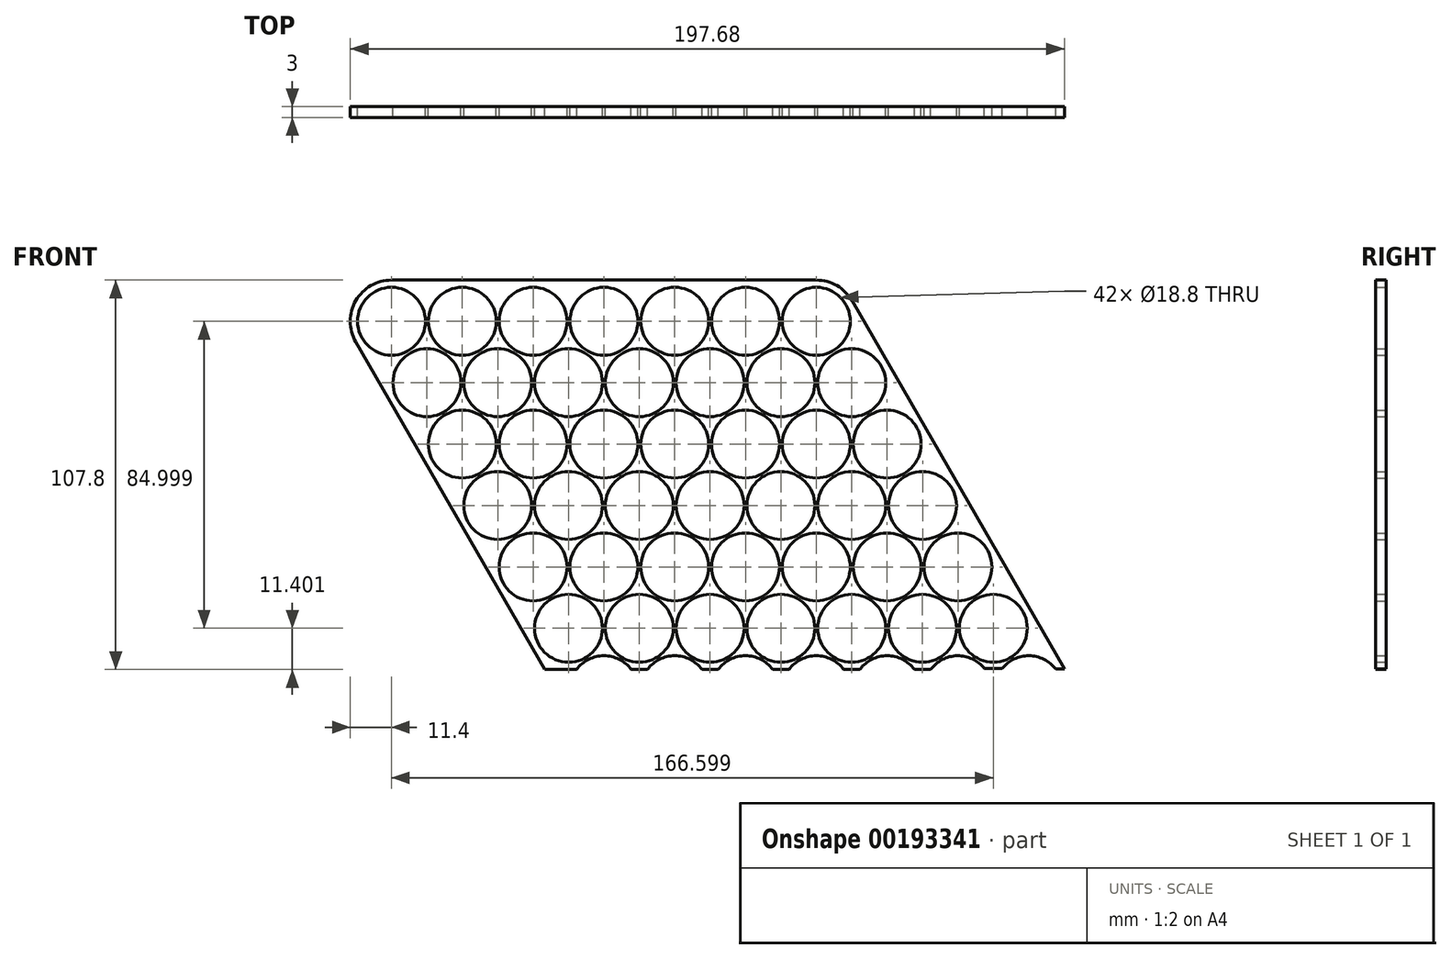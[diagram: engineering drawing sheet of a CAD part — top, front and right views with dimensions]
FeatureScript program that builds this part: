
annotation { "Feature Type Name" : "Feature", "Feature Type Description" : "" }
export const myFeature = defineFeature(function(context is Context, id is Id, definition is map)
    precondition{}
    {
        {
            var Q0;
            Q0=qCreatedBy(makeId("Front.planeOp"),FACE);
            var sketch = newSketch(context, id + "F0", { "sketchPlane" : qUnion([Q0])});
            skCircle(sketch, "E0", {"center": v(0, 0) * mm, "radius": 9.4 * mm});
            skCircle(sketch, "E1.1.0.0", {"center": v(19.6, 0) * mm, "radius": 9.4 * mm});
            skCircle(sketch, "E1.2.0.0", {"center": v(39.2, 0) * mm, "radius": 9.4 * mm});
            skCircle(sketch, "E1.3.0.0", {"center": v(58.8, 0) * mm, "radius": 9.4 * mm});
            skLineSegment(sketch, "E1.direction1", {"start": v(0, 0) * mm, "end": v(19.6, 0) * mm, "construction": true});
            skLineSegment(sketch, "E2", {"start": v(0, -17) * mm, "end": v(73.2, -17) * mm, "construction": true});
            skLineSegment(sketch, "E3", {"start": v(9.8, 0) * mm, "end": v(9.8, -17) * mm, "construction": true});
            skCircle(sketch, "E4", {"center": v(9.8, -17) * mm, "radius": 9.4 * mm});
            skCircle(sketch, "E5.1.0.0", {"center": v(29.4, -17) * mm, "radius": 9.4 * mm});
            skCircle(sketch, "E5.2.0.0", {"center": v(49, -17) * mm, "radius": 9.4 * mm});
            skCircle(sketch, "E5.3.0.0", {"center": v(68.6, -17) * mm, "radius": 9.4 * mm});
            skLineSegment(sketch, "E5.direction1", {"start": v(9.8, -17) * mm, "end": v(29.4, -17) * mm, "construction": true});
            skLineSegment(sketch, "E6", {"start": v(9.8, -17) * mm, "end": v(9.8, -26.4) * mm, "construction": true});
            skLineSegment(sketch, "E7", {"start": v(68.6, -17) * mm, "end": v(68.6, -26.4) * mm, "construction": true});
            skArc(sketch, "E8", {"start": v(58.8, 9.4) * mm, "mid": v(63.5, 8.14) * mm, "end": v(66.94, 4.7) * mm});
            skArc(sketch, "E9", {"start": v(76.74, -12.3) * mm, "mid": v(76.74, -21.7) * mm, "end": v(68.6, -26.4) * mm});
            skArc(sketch, "E10", {"start": v(9.8, -26.4) * mm, "mid": v(5.1, -25.14) * mm, "end": v(1.66, -21.7) * mm});
            skArc(sketch, "E11", {"start": v(-8.14, -4.7) * mm, "mid": v(-8.14, 4.7) * mm, "end": v(0, 9.4) * mm});
            skArc(sketch, "E12.0", {"start": v(0, 11.4) * mm, "mid": v(-9.87, 5.7) * mm, "end": v(-9.88, -5.7) * mm});
            skLineSegment(sketch, "E13.0", {"start": v(0, 11.4) * mm, "end": v(58.8, 11.4) * mm});
            skLineSegment(sketch, "E14.0", {"start": v(-9.88, -5.7) * mm, "end": v(-0.08, -22.7) * mm});
            skArc(sketch, "E15.trimOffspring", {"start": v(9.8, -5.82) * mm, "mid": v(9.87, -5.71) * mm, "end": v(9.93, -5.6) * mm});
            skArc(sketch, "E16.trimOffspring", {"start": v(9.93, -5.6) * mm, "mid": v(9.86, -5.6) * mm, "end": v(9.8, -5.6) * mm});
            skCircle(sketch, "E17.0.4.0", {"center": v(78.4, 0) * mm, "radius": 9.4 * mm});
            skCircle(sketch, "E17.0.5.0", {"center": v(98, 0) * mm, "radius": 9.4 * mm});
            skCircle(sketch, "E18.0.4.0", {"center": v(88.2, -17) * mm, "radius": 9.4 * mm});
            skCircle(sketch, "E18.0.5.0", {"center": v(107.8, -17) * mm, "radius": 9.4 * mm});
            skLineSegment(sketch, "E19", {"start": v(58.8, 11.4) * mm, "end": v(98, 11.4) * mm});
            skLineSegment(sketch, "E20", {"start": v(0, 0) * mm, "end": v(9.8, -17) * mm, "construction": true});
            skCircle(sketch, "E21.1.0.0", {"center": v(19.6, -34) * mm, "radius": 9.4 * mm});
            skCircle(sketch, "E21.2.0.0", {"center": v(29.4, -51) * mm, "radius": 9.4 * mm});
            skLineSegment(sketch, "E21.direction1", {"start": v(9.8, -17) * mm, "end": v(19.6, -34) * mm, "construction": true});
            skCircle(sketch, "E22.1.0.0", {"center": v(39.2, -34) * mm, "radius": 9.4 * mm});
            skCircle(sketch, "E22.1.0.1", {"center": v(49, -51) * mm, "radius": 9.4 * mm});
            skCircle(sketch, "E22.2.0.0", {"center": v(58.8, -34) * mm, "radius": 9.4 * mm});
            skCircle(sketch, "E22.2.0.1", {"center": v(68.6, -51) * mm, "radius": 9.4 * mm});
            skCircle(sketch, "E22.3.0.0", {"center": v(78.4, -34) * mm, "radius": 9.4 * mm});
            skCircle(sketch, "E22.3.0.1", {"center": v(88.2, -51) * mm, "radius": 9.4 * mm});
            skCircle(sketch, "E22.4.0.0", {"center": v(98, -34) * mm, "radius": 9.4 * mm});
            skCircle(sketch, "E22.4.0.1", {"center": v(107.8, -51) * mm, "radius": 9.4 * mm});
            skCircle(sketch, "E22.5.0.0", {"center": v(117.6, -34) * mm, "radius": 9.4 * mm});
            skCircle(sketch, "E22.5.0.1", {"center": v(127.4, -51) * mm, "radius": 9.4 * mm});
            skLineSegment(sketch, "E22.direction1", {"start": v(19.6, -34) * mm, "end": v(39.2, -34) * mm, "construction": true});
            skLineSegment(sketch, "E23", {"start": v(-0.08, -22.7) * mm, "end": v(19.52, -56.7) * mm});
            skArc(sketch, "E24.0", {"start": v(29.27, -62.4) * mm, "mid": v(29.33, -62.4) * mm, "end": v(29.4, -62.4) * mm});
            skCircle(sketch, "E25.0.6.0", {"center": v(117.6, 0) * mm, "radius": 9.4 * mm});
            skCircle(sketch, "E26.0.6.0", {"center": v(127.4, -17) * mm, "radius": 9.4 * mm});
            skCircle(sketch, "E27.0.6.0", {"center": v(137.2, -34) * mm, "radius": 9.4 * mm});
            skCircle(sketch, "E27.2.6.0", {"center": v(147, -51) * mm, "radius": 9.4 * mm});
            skLineSegment(sketch, "E28", {"start": v(98, 11.4) * mm, "end": v(117.6, 11.4) * mm});
            skCircle(sketch, "E29.0.3.0", {"center": v(39.2, -68) * mm, "radius": 9.4 * mm});
            skCircle(sketch, "E30.1.0.0", {"center": v(58.8, -68) * mm, "radius": 9.4 * mm});
            skCircle(sketch, "E30.2.0.0", {"center": v(78.4, -68) * mm, "radius": 9.4 * mm});
            skCircle(sketch, "E30.3.0.0", {"center": v(98, -68) * mm, "radius": 9.4 * mm});
            skCircle(sketch, "E30.4.0.0", {"center": v(117.6, -68) * mm, "radius": 9.4 * mm});
            skCircle(sketch, "E30.5.0.0", {"center": v(137.2, -68) * mm, "radius": 9.4 * mm});
            skCircle(sketch, "E30.6.0.0", {"center": v(156.8, -68) * mm, "radius": 9.4 * mm});
            skLineSegment(sketch, "E30.direction1", {"start": v(39.2, -68) * mm, "end": v(58.8, -68) * mm, "construction": true});
            skArc(sketch, "E31.0", {"start": v(39.07, -79.4) * mm, "mid": v(39.13, -79.4) * mm, "end": v(39.2, -79.4) * mm});
            skLineSegment(sketch, "E32", {"start": v(19.52, -56.7) * mm, "end": v(29.32, -73.7) * mm});
            skArc(sketch, "E33", {"start": v(127.48, 5.7) * mm, "mid": v(123.3, 9.87) * mm, "end": v(117.6, 11.4) * mm});
            skLineSegment(sketch, "E34", {"start": v(127.48, 5.7) * mm, "end": v(166.68, -62.3) * mm});
            skCircle(sketch, "E35.0.4.0", {"center": v(49, -85) * mm, "radius": 9.4 * mm});
            skArc(sketch, "E35.0.5.0", {"start": v(66.35, -96.4) * mm, "mid": v(58.8, -92.6) * mm, "end": v(51.25, -96.4) * mm});
            skCircle(sketch, "E36.1.0.0", {"center": v(68.6, -85) * mm, "radius": 9.4 * mm});
            skArc(sketch, "E36.1.0.1", {"start": v(85.95, -96.4) * mm, "mid": v(78.4, -92.6) * mm, "end": v(70.85, -96.4) * mm});
            skCircle(sketch, "E36.2.0.0", {"center": v(88.2, -85) * mm, "radius": 9.4 * mm});
            skArc(sketch, "E36.2.0.1", {"start": v(105.55, -96.4) * mm, "mid": v(98, -92.6) * mm, "end": v(90.45, -96.4) * mm});
            skCircle(sketch, "E36.3.0.0", {"center": v(107.8, -85) * mm, "radius": 9.4 * mm});
            skArc(sketch, "E36.3.0.1", {"start": v(125.15, -96.4) * mm, "mid": v(117.6, -92.6) * mm, "end": v(110.05, -96.4) * mm});
            skCircle(sketch, "E36.4.0.0", {"center": v(127.4, -85) * mm, "radius": 9.4 * mm});
            skArc(sketch, "E36.4.0.1", {"start": v(144.75, -96.4) * mm, "mid": v(137.2, -92.6) * mm, "end": v(129.65, -96.4) * mm});
            skCircle(sketch, "E36.5.0.0", {"center": v(147, -85) * mm, "radius": 9.4 * mm});
            skArc(sketch, "E36.5.0.1", {"start": v(164.14, -96.13) * mm, "mid": v(156.63, -92.6) * mm, "end": v(149.25, -96.4) * mm});
            skCircle(sketch, "E36.6.0.0", {"center": v(166.6, -85) * mm, "radius": 9.4 * mm});
            skArc(sketch, "E36.6.0.1", {"start": v(175, -92.7) * mm, "mid": v(171.7, -93.85) * mm, "end": v(169.05, -96.13) * mm});
            skLineSegment(sketch, "E36.direction1", {"start": v(49, -85) * mm, "end": v(68.6, -85) * mm, "construction": true});
            skLineSegment(sketch, "E37", {"start": v(29.32, -73.7) * mm, "end": v(39.12, -90.7) * mm});
            skLineSegment(sketch, "E38", {"start": v(49, -96.4) * mm, "end": v(51.25, -96.4) * mm});
            skLineSegment(sketch, "E39.trimOffspring", {"start": v(66.35, -96.4) * mm, "end": v(70.85, -96.4) * mm});
            skLineSegment(sketch, "E40.trimOffspring", {"start": v(85.95, -96.4) * mm, "end": v(90.45, -96.4) * mm});
            skLineSegment(sketch, "E41.trimOffspring", {"start": v(105.55, -96.4) * mm, "end": v(110.05, -96.4) * mm});
            skLineSegment(sketch, "E42.trimOffspring", {"start": v(125.15, -96.4) * mm, "end": v(129.65, -96.4) * mm});
            skLineSegment(sketch, "E43.trimOffspring", {"start": v(144.75, -96.4) * mm, "end": v(149.25, -96.4) * mm});
            skLineSegment(sketch, "E44.trimOffspring", {"start": v(156.67, -79.4) * mm, "end": v(156.8, -79.4) * mm});
            skLineSegment(sketch, "E45", {"start": v(164.14, -96.13) * mm, "end": v(169.05, -96.13) * mm});
            skLineSegment(sketch, "E46", {"start": v(166.68, -62.3) * mm, "end": v(176.48, -79.3) * mm});
            skArc(sketch, "E47", {"start": v(183.74, -96.13) * mm, "mid": v(176.4, -92.6) * mm, "end": v(169.05, -96.13) * mm});
            skArc(sketch, "E48", {"start": v(183.86, -96.28) * mm, "mid": v(176.5, -92.6) * mm, "end": v(169.05, -96.13) * mm});
            skLineSegment(sketch, "E49", {"start": v(176.48, -79.3) * mm, "end": v(186.28, -96.3) * mm});
            skLineSegment(sketch, "E50", {"start": v(183.86, -96.28) * mm, "end": v(186.28, -96.3) * mm});
            skLineSegment(sketch, "E51", {"start": v(49, -96.4) * mm, "end": v(42.41, -96.4) * mm});
            skLineSegment(sketch, "E52", {"start": v(39.12, -90.7) * mm, "end": v(42.41, -96.4) * mm});
            skSolve(sketch);
        }
        {
            var Q0;
            Q0=qSketchRegion(id+"F0",true);
            var Q1;
            {var subQ3=sQuery(id+"F0.wireOp",EDGE,"E1.1.0.0");Q1=makeQuery(id+"F0.imprint","IMPRINT",FACE,{"disambiguationData":[TD([[makeQuery(id+"F0.imprint","IMPRINT",EDGE,{"derivedFrom":subQ3}),-1.0]])]});}
            extrude(context, id + "F1", {"entities" : qUnion([Q0, Q1]), "depth" : 3 * mm});
        }
    });
